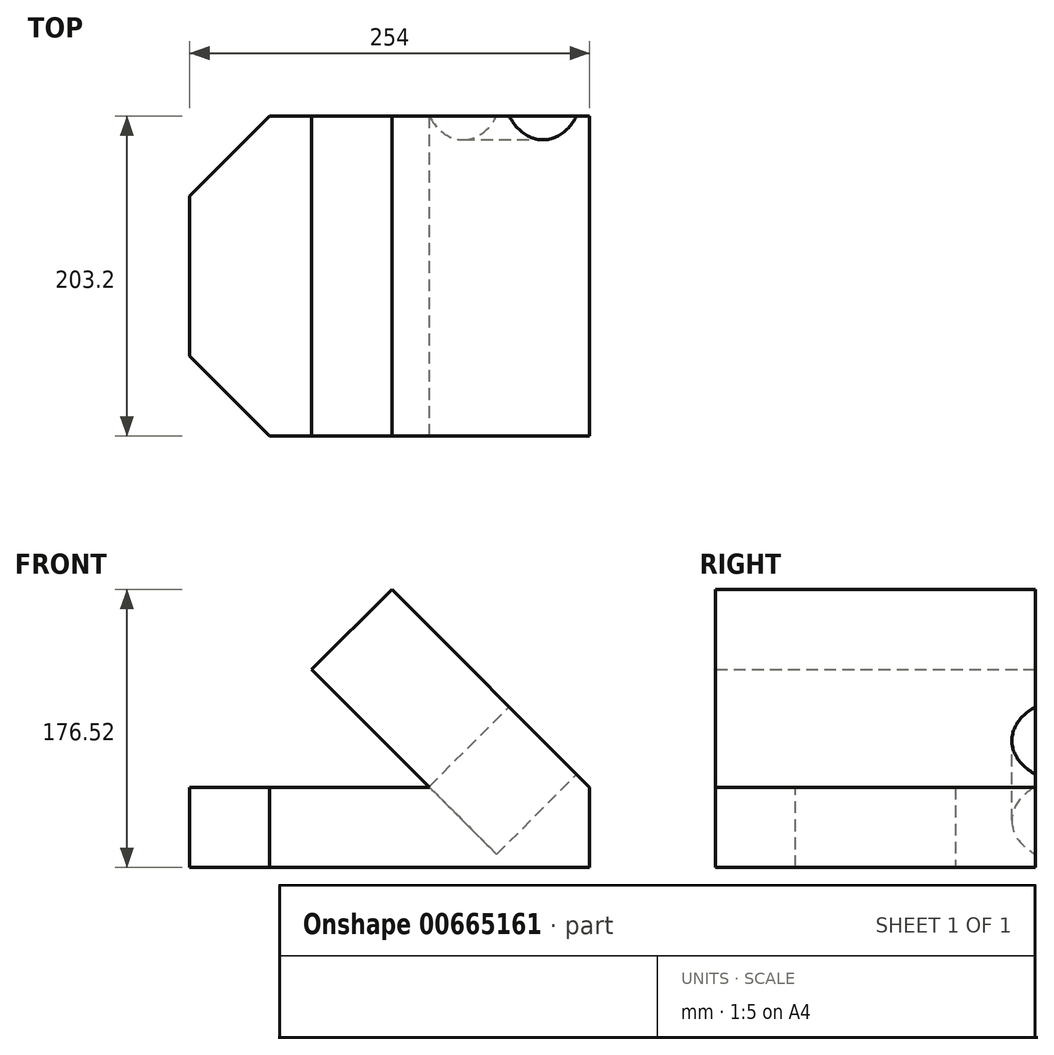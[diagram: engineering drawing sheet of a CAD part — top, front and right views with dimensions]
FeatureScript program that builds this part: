
annotation { "Feature Type Name" : "Feature", "Feature Type Description" : "" }
export const myFeature = defineFeature(function(context is Context, id is Id, definition is map)
    precondition{}
    {
        {
            var Q0;
            Q0=qCreatedBy(makeId("Front.planeOp"),FACE);
            var sketch = newSketch(context, id + "F0", { "sketchPlane" : qUnion([Q0])});
            skLineSegment(sketch, "E0", {"start": v(0, 0) * mm, "end": v(254, 0) * mm});
            skLineSegment(sketch, "E1", {"start": v(254, 0) * mm, "end": v(254, 50.8) * mm});
            skLineSegment(sketch, "E2", {"start": v(254, 50.8) * mm, "end": v(128.28, 176.52) * mm});
            skLineSegment(sketch, "E3", {"start": v(128.28, 176.52) * mm, "end": v(77.48, 125.72) * mm});
            skLineSegment(sketch, "E4", {"start": v(77.48, 125.72) * mm, "end": v(152.4, 50.8) * mm});
            skLineSegment(sketch, "E5", {"start": v(152.4, 50.8) * mm, "end": v(0, 50.8) * mm});
            skLineSegment(sketch, "E6", {"start": v(0, 50.8) * mm, "end": v(0, 0) * mm});
            skSolve(sketch);
        }
        {
            var Q0;
            Q0 = qSketchRegion(id + "F0", true);
            extrude(context, id + "F1", {"entities" : qUnion([Q0]), "depth" : 203.2 * mm, "offsetDistance" : 25.4 * mm});
        }
        {
            var Q0;
            Q0=makeQuery(id+"F1.opExtrude","SWEPT_FACE",FACE,{"disambiguationData":[OSD([sQuery(id+"F0.wireOp",EDGE,"E2")])]});
            var sketch = newSketch(context, id + "F2", { "sketchPlane" : qUnion([Q0])});
            skCircle(sketch, "E7", {"center": v(23.03, -101.6) * mm, "radius": 38.1 * mm});
            skSolve(sketch);
        }
        {
            var Q0;
            Q0=makeQuery(id+"F2.imprint","IMPRINT",FACE,{"disambiguationData":[TD([[makeQuery(id+"F2.imprint","IMPRINT",EDGE,{"derivedFrom":sQuery(id+"F2.wireOp",EDGE,"E7")}),1.0]])]});
            extrude(context, id + "F3", {"entities" : qUnion([Q0]), "operationType" : NewBodyOperationType.REMOVE, "oppositeDirection" : true, "depth" : 71.84 * mm, "offsetDistance" : 25.4 * mm});
        }
        {
            var Q0;
            Q0=makeQuery(id+"F1.opExtrude","CAP_EDGE",EDGE,{"disambiguationData":[OSD([sQuery(id+"F0.wireOp",EDGE,"E6")])],"isStart":true});
            var Q1;
            Q1=makeQuery(id+"F1.opExtrude","CAP_EDGE",EDGE,{"disambiguationData":[OSD([sQuery(id+"F0.wireOp",EDGE,"E6")])],"isStart":false});
            chamfer(context, id + "F4", {"entities" : qUnion([Q0, Q1]), "width" : 50.8 * mm, "tangentPropagation" : true});
        }
    });
